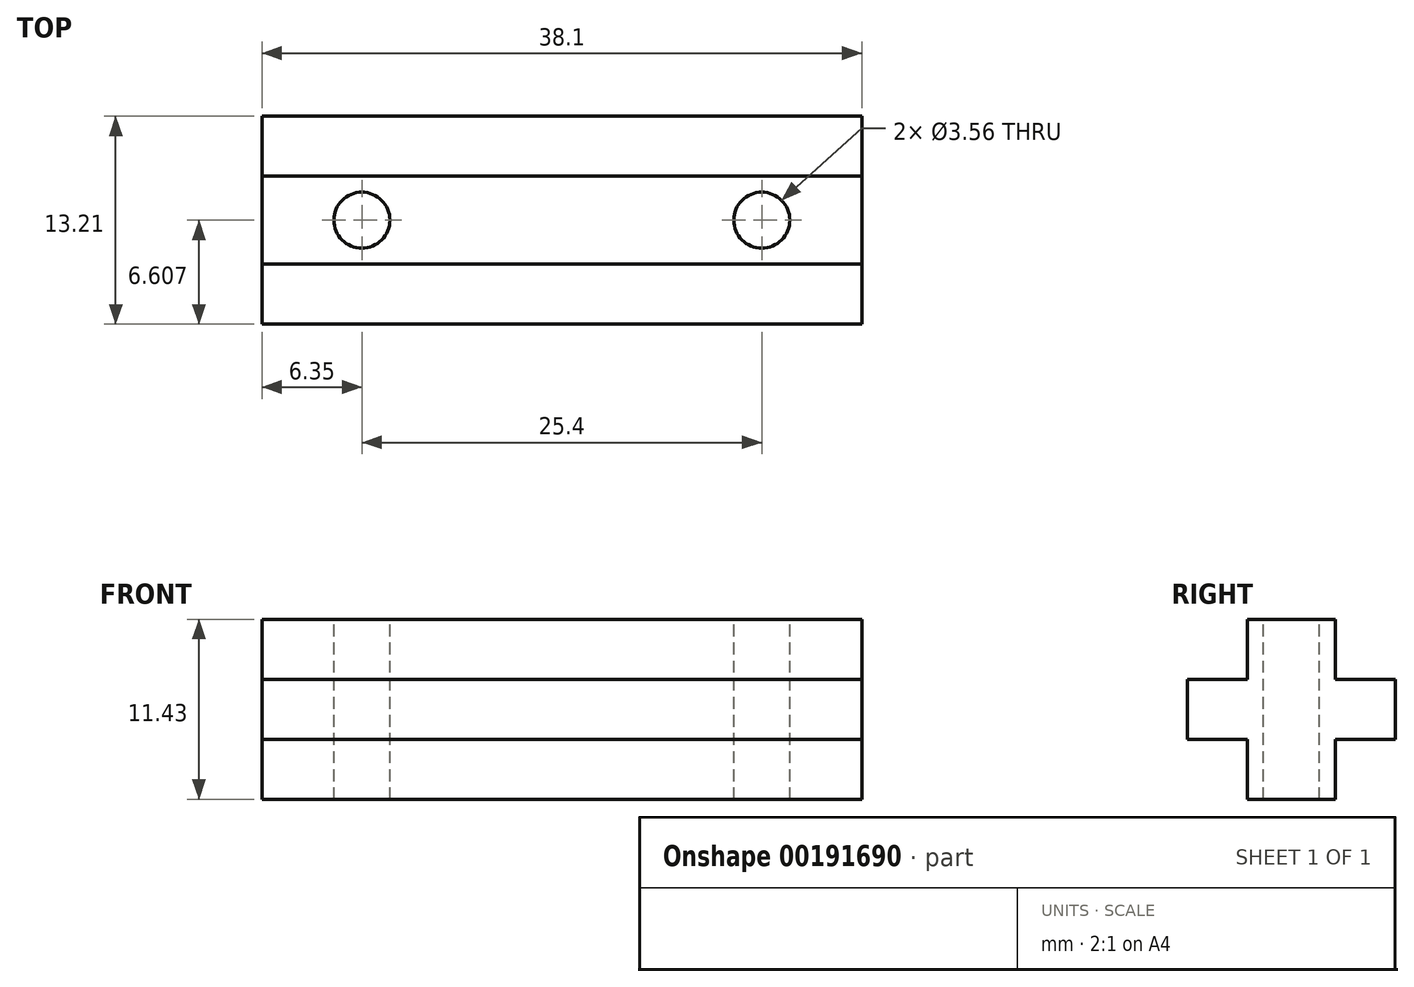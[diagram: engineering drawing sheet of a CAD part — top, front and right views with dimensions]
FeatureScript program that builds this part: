
annotation { "Feature Type Name" : "Feature", "Feature Type Description" : "" }
export const myFeature = defineFeature(function(context is Context, id is Id, definition is map)
    precondition{}
    {
        {
            var Q0;
            Q0=qCreatedBy(makeId("Right.planeOp"),FACE);
            var sketch = newSketch(context, id + "F0", { "sketchPlane" : qUnion([Q0])});
            skLineSegment(sketch, "E0", {"start": v(-1.2, -22.4) * mm, "end": v(4.38, -22.4) * mm});
            skLineSegment(sketch, "E1", {"start": v(4.38, -22.4) * mm, "end": v(4.38, -18.6) * mm});
            skLineSegment(sketch, "E2", {"start": v(4.38, -18.6) * mm, "end": v(8.2, -18.6) * mm});
            skLineSegment(sketch, "E3", {"start": v(8.2, -18.6) * mm, "end": v(8.2, -14.79) * mm});
            skLineSegment(sketch, "E4", {"start": v(8.2, -14.79) * mm, "end": v(4.38, -14.79) * mm});
            skLineSegment(sketch, "E5", {"start": v(4.38, -14.79) * mm, "end": v(4.38, -10.98) * mm});
            skLineSegment(sketch, "E6", {"start": v(4.38, -10.98) * mm, "end": v(-1.2, -10.98) * mm});
            skLineSegment(sketch, "E7", {"start": v(-1.2, -10.98) * mm, "end": v(-1.2, -14.79) * mm});
            skLineSegment(sketch, "E8", {"start": v(-1.2, -14.79) * mm, "end": v(-5.02, -14.79) * mm});
            skLineSegment(sketch, "E9", {"start": v(-5.02, -14.79) * mm, "end": v(-5.02, -18.6) * mm});
            skLineSegment(sketch, "E10", {"start": v(-5.02, -18.6) * mm, "end": v(-1.2, -18.6) * mm});
            skLineSegment(sketch, "E11", {"start": v(-1.2, -18.6) * mm, "end": v(-1.2, -22.4) * mm});
            skSolve(sketch);
        }
        {
            var Q0;
            Q0=makeQuery(id+"F0.imprint","IMPRINT",FACE,{"disambiguationData":[TD([[makeQuery(id+"F0.imprint","IMPRINT",EDGE,{"derivedFrom":sQuery(id+"F0.wireOp",EDGE,"E0")}),1.0]])]});
            extrude(context, id + "F1", {"entities" : qUnion([Q0]), "depth" : 38.1 * mm});
        }
        {
            var Q0;
            Q0=makeQuery(id+"F1.opExtrude","SWEPT_FACE",FACE,{"disambiguationData":[OSD([sQuery(id+"F0.wireOp",EDGE,"E6")])]});
            var sketch = newSketch(context, id + "F2", { "sketchPlane" : qUnion([Q0])});
            skCircle(sketch, "E12", {"center": v(6.35, 1.59) * mm, "radius": 1.78 * mm});
            skPoint(sketch, "E12.centerSnap0", {"position": v(0, 1.59) * mm});
            skCircle(sketch, "E13", {"center": v(31.75, 1.59) * mm, "radius": 1.78 * mm});
            skSolve(sketch);
        }
        {
            var Q0;
            Q0=qSketchRegion(id+"F2",true);
            extrude(context, id + "F3", {"entities" : qUnion([Q0]), "operationType" : NewBodyOperationType.REMOVE, "oppositeDirection" : true, "depth" : 25.4 * mm});
        }
    });
